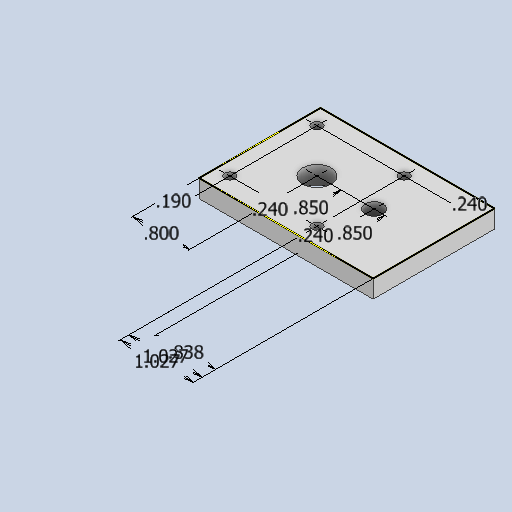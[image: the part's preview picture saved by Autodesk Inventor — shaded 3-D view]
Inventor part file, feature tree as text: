
AUTODESK INVENTOR PART (.ipt)
format: ipt  version: 2025.1 (Build 291241020, 241B)  size: 144,896 bytes
history: native  units: in
note: dims shown in document units (in); Inventor stores cm internally (conversion verified against a paired STEP export)
features: hole x4, sketch x3, extrude x1
ambient origin geometry x8: Origin, YZ Plane, XZ Plane, XY Plane, X Axis, Y Axis, Z Axis, Center Point
bodies: Solid1 (feature_tree)
feature tree (8):
  extrude  "Extrusion1"  Depth=1.7in
  sketch  "Sketch2"  dims[d2=0.25in d3=0.0in d4=0.2398in]
  hole  "Hole1"  [1 undecoded]
  hole  "Hole2"  [1 undecoded]
  hole  "Hole3"  [1 undecoded]
  hole  "Hole4"  [1 undecoded]
  sketch  "Sketch1"  dims[d0=2.4375in d1=1.7in]
  sketch  "Sketch3"  dims[d5=0.1898in d6=0.2398in d7=0.1898in d8=0.2398in d9=1.0273in d10=0.8375in d11=0.85in d12=0.2398in d13=1.0273in d14=0.85in d15=0.8in d16=0.142in d17=0.276in d18=0.375in d19=0.25in d20=0.5635in d21=0.432in d22=0.8108in d23=0.3976in d24=0.75in d25=0.375in d26=0.25in d27=0.5635in d28=0.432in d29=0.8108in d30=0.104in d31=0.276in d32=0.279in d33=0.25in d34=0.5635in d35=0.5in d36=0.8108in d37=0.45in d38=0.45in d39=0.125in d40=0.25in d41=0.75in d42=0.375in d43=0.25in d44=0.5635in d45=0.432in d46=0.8108in]
note: 4 required parameter values undecoded (feature->parameter linkage not recoverable at this tier; creation-order binding heuristic only, values carry confidence <= 0.55)
